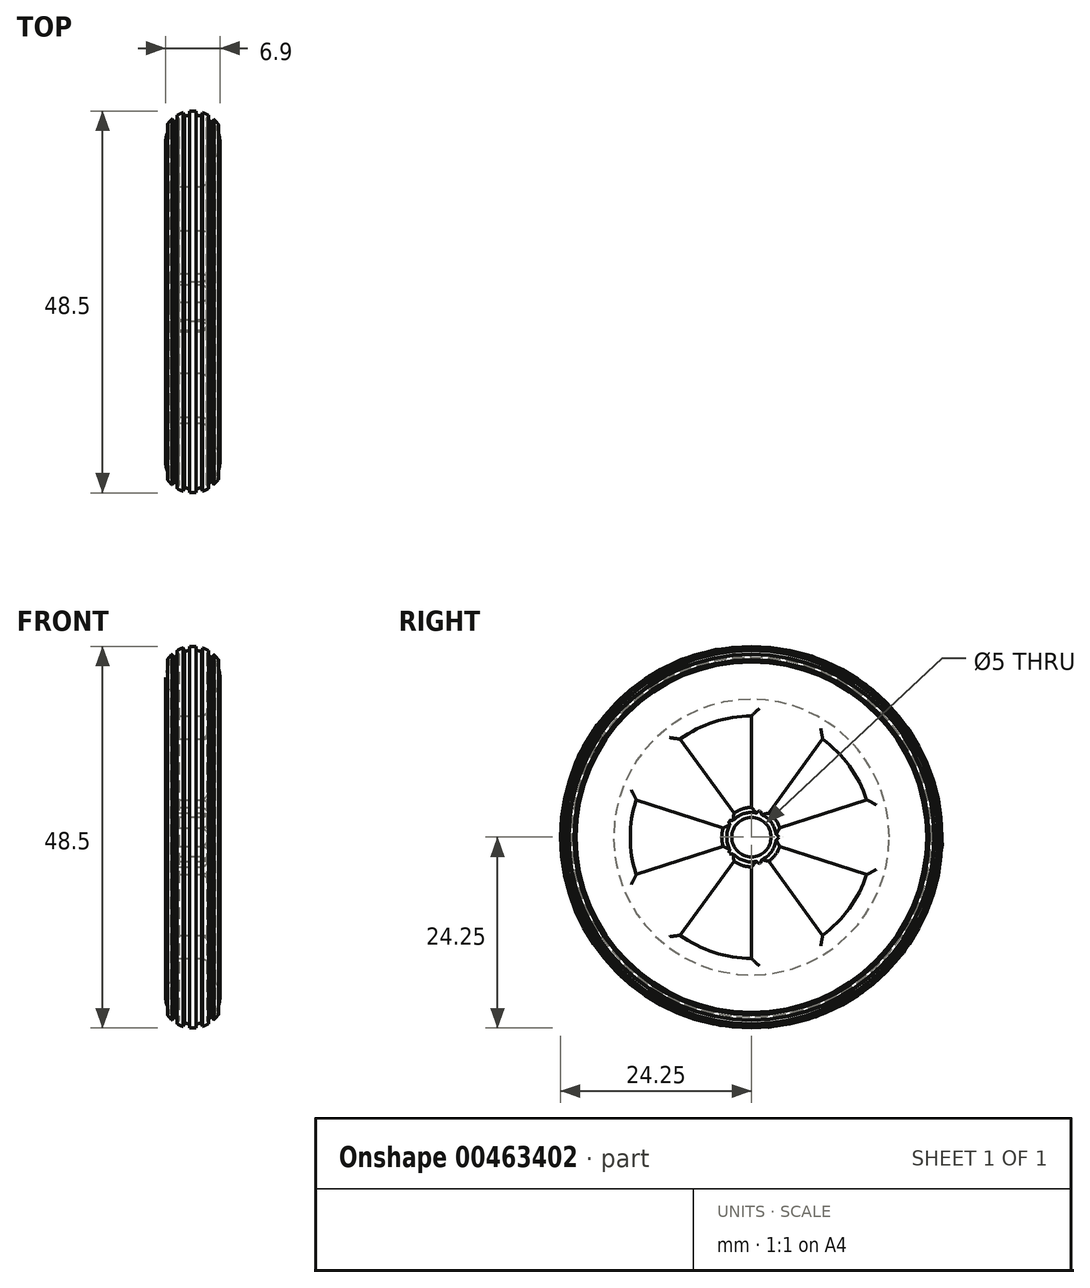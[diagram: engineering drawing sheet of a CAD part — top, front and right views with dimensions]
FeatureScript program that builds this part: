
annotation { "Feature Type Name" : "Feature", "Feature Type Description" : "" }
export const myFeature = defineFeature(function(context is Context, id is Id, definition is map)
    precondition{}
    {
        {
            var Q0;
            Q0=qCreatedBy(makeId("Front.planeOp"),FACE);
            var sketch = newSketch(context, id + "F0", { "sketchPlane" : qUnion([Q0])});
            skLineSegment(sketch, "E0", {"start": v(0, 0) * mm, "end": v(0, 2.5) * mm});
            skLineSegment(sketch, "E1", {"start": v(0, 2.5) * mm, "end": v(4, 2.5) * mm});
            skLineSegment(sketch, "E2", {"start": v(0, 2.5) * mm, "end": v(0, 17.5) * mm});
            skLineSegment(sketch, "E3", {"start": v(4, 2.5) * mm, "end": v(4, 17.5) * mm});
            skArc(sketch, "E4", {"start": v(4, 17.5) * mm, "mid": v(5.4, 19.71) * mm, "end": v(4.84, 22.27) * mm});
            skPoint(sketch, "E4.third.point", {"position": v(4, 23.12) * mm});
            skArc(sketch, "E5", {"start": v(-0.65, 23.22) * mm, "mid": v(-0.95, 22.92) * mm, "end": v(-1.21, 22.6) * mm});
            skLineSegment(sketch, "E6", {"start": v(-0.8, 22.3) * mm, "end": v(-1.21, 22.6) * mm});
            skLineSegment(sketch, "E7.1.0", {"start": v(-0.32, 22.86) * mm, "end": v(-0.65, 23.22) * mm});
            skLineSegment(sketch, "E7.2.0", {"start": v(0.27, 23.3) * mm, "end": v(0.02, 23.72) * mm});
            skLineSegment(sketch, "E7.3.0", {"start": v(0.94, 23.59) * mm, "end": v(0.79, 24.06) * mm});
            skLineSegment(sketch, "E7.4.0", {"start": v(1.66, 23.74) * mm, "end": v(1.6, 24.23) * mm});
            skLineSegment(sketch, "E7.5.0", {"start": v(2.4, 23.73) * mm, "end": v(2.45, 24.22) * mm});
            skLineSegment(sketch, "E7.6.0", {"start": v(3.1, 23.57) * mm, "end": v(3.27, 24.04) * mm});
            skLineSegment(sketch, "E7.7.0", {"start": v(3.77, 23.26) * mm, "end": v(4.03, 23.69) * mm});
            skLineSegment(sketch, "E7.8.0", {"start": v(4.36, 22.82) * mm, "end": v(4.7, 23.18) * mm});
            skLineSegment(sketch, "E7.9.0", {"start": v(4.84, 22.27) * mm, "end": v(5.24, 22.54) * mm});
            skLineSegment(sketch, "E7.anchor1", {"start": v(-0.8, 22.3) * mm, "end": v(-1.21, 22.6) * mm, "construction": true});
            skLineSegment(sketch, "E7.anchor2", {"start": v(4.84, 22.27) * mm, "end": v(5.24, 22.54) * mm, "construction": true});
            skArc(sketch, "E8.trimOffspring", {"start": v(0.79, 24.06) * mm, "mid": v(0.4, 23.9) * mm, "end": v(0.02, 23.72) * mm});
            skArc(sketch, "E9.trimOffspring", {"start": v(2.45, 24.22) * mm, "mid": v(2.03, 24.25) * mm, "end": v(1.6, 24.23) * mm});
            skArc(sketch, "E10.trimOffspring", {"start": v(4.03, 23.69) * mm, "mid": v(3.66, 23.88) * mm, "end": v(3.27, 24.04) * mm});
            skArc(sketch, "E11.trimOffspring", {"start": v(-0.8, 22.3) * mm, "mid": v(-1.4, 19.74) * mm, "end": v(0, 17.5) * mm});
            skArc(sketch, "E12.trimOffspring", {"start": v(0.27, 23.3) * mm, "mid": v(-0.04, 23.09) * mm, "end": v(-0.32, 22.86) * mm});
            skArc(sketch, "E13.trimOffspring", {"start": v(1.66, 23.74) * mm, "mid": v(1.3, 23.68) * mm, "end": v(0.94, 23.59) * mm});
            skArc(sketch, "E14.trimOffspring", {"start": v(3.1, 23.57) * mm, "mid": v(2.75, 23.67) * mm, "end": v(2.4, 23.73) * mm});
            skArc(sketch, "E15.trimOffspring", {"start": v(4.36, 22.82) * mm, "mid": v(4.08, 23.06) * mm, "end": v(3.77, 23.26) * mm});
            skArc(sketch, "E16.trimOffspring", {"start": v(5.24, 22.54) * mm, "mid": v(4.99, 22.88) * mm, "end": v(4.7, 23.18) * mm});
            skLineSegment(sketch, "E17", {"start": v(0, 0) * mm, "end": v(4.13, 0) * mm});
            skSolve(sketch);
        }
        {
            var Q0;
            Q0=makeQuery(id+"F0.imprint","IMPRINT",FACE,{"disambiguationData":[TD([[makeQuery(id+"F0.imprint","IMPRINT",EDGE,{"derivedFrom":sQuery(id+"F0.wireOp",EDGE,"E1")}),1.0]])]});
            var Q1;
            Q1=sQuery(id+"F0.wireOp",EDGE,"E17");
            revolve(context, id + "F1", {"entities" : qUnion([Q0]), "axis" : qUnion([Q1]), "revolveType" : RevolveType.FULL});
        }
        {
            var Q0;
            Q0=makeQuery(id+"F1.opRevolve","SWEPT_FACE",FACE,{"disambiguationData":[OSD([sQuery(id+"F0.wireOp",EDGE,"E3")])]});
            var sketch = newSketch(context, id + "F2", { "sketchPlane" : qUnion([Q0])});
            skArc(sketch, "E18", {"start": v(0, 15.39) * mm, "mid": v(-4.76, 14.64) * mm, "end": v(-9.05, 12.45) * mm});
            skArc(sketch, "E19", {"start": v(0, 3.77) * mm, "mid": v(-1.17, 3.59) * mm, "end": v(-2.22, 3.05) * mm});
            skLineSegment(sketch, "E20", {"start": v(0, 3.77) * mm, "end": v(0, 15.39) * mm});
            skLineSegment(sketch, "E21.1.0", {"start": v(-2.22, 3.05) * mm, "end": v(-9.05, 12.45) * mm});
            skLineSegment(sketch, "E21.2.0", {"start": v(-3.59, 1.17) * mm, "end": v(-14.64, 4.76) * mm});
            skLineSegment(sketch, "E21.3.0", {"start": v(-3.59, -1.17) * mm, "end": v(-14.64, -4.76) * mm});
            skLineSegment(sketch, "E21.4.0", {"start": v(-2.22, -3.05) * mm, "end": v(-9.05, -12.45) * mm});
            skLineSegment(sketch, "E21.5.0", {"start": v(0, -3.77) * mm, "end": v(0, -15.39) * mm});
            skLineSegment(sketch, "E21.6.0", {"start": v(2.22, -3.05) * mm, "end": v(9.05, -12.45) * mm});
            skLineSegment(sketch, "E21.7.0", {"start": v(3.59, -1.17) * mm, "end": v(14.64, -4.76) * mm});
            skLineSegment(sketch, "E21.8.0", {"start": v(3.59, 1.17) * mm, "end": v(14.64, 4.76) * mm});
            skLineSegment(sketch, "E21.9.0", {"start": v(2.22, 3.05) * mm, "end": v(9.05, 12.45) * mm});
            skArc(sketch, "E22.trimOffspring", {"start": v(3.59, 1.17) * mm, "mid": v(3.05, 2.22) * mm, "end": v(2.22, 3.05) * mm});
            skArc(sketch, "E23.trimOffspring", {"start": v(14.64, 4.76) * mm, "mid": v(12.45, 9.05) * mm, "end": v(9.05, 12.45) * mm});
            skArc(sketch, "E24.trimOffspring", {"start": v(2.22, -3.05) * mm, "mid": v(3.05, -2.22) * mm, "end": v(3.59, -1.17) * mm});
            skArc(sketch, "E25.trimOffspring", {"start": v(9.05, -12.45) * mm, "mid": v(12.45, -9.05) * mm, "end": v(14.64, -4.76) * mm});
            skArc(sketch, "E26.trimOffspring", {"start": v(-2.22, -3.05) * mm, "mid": v(-1.17, -3.59) * mm, "end": v(0, -3.77) * mm});
            skArc(sketch, "E27.trimOffspring", {"start": v(-9.05, -12.45) * mm, "mid": v(-4.76, -14.64) * mm, "end": v(0, -15.39) * mm});
            skArc(sketch, "E28.trimOffspring", {"start": v(-3.59, 1.17) * mm, "mid": v(-3.77, 0) * mm, "end": v(-3.59, -1.17) * mm});
            skArc(sketch, "E29.trimOffspring", {"start": v(-14.64, 4.76) * mm, "mid": v(-15.39, 0) * mm, "end": v(-14.64, -4.76) * mm});
            skSolve(sketch);
        }
        {
            var Q0;
            Q0 = qSketchRegion(id + "F2", true);
            extrude(context, id + "F3", {"entities" : qUnion([Q0]), "operationType" : NewBodyOperationType.REMOVE, "oppositeDirection" : true, "depth" : 4 * mm});
        }
        {
            var Q0;
            Q0=makeQuery(id+"F3.boolean.opBoolean","COPY",EDGE,{"derivedFrom":makeQuery(id+"F3.opExtrude","CAP_EDGE",EDGE,{"disambiguationData":[OSD([sQuery(id+"F2.wireOp",EDGE,"E29.trimOffspring")])],"isStart":true})});
            var Q1;
            Q1=makeQuery(id+"F3.boolean.opBoolean","COPY",EDGE,{"derivedFrom":makeQuery(id+"F3.opExtrude","CAP_EDGE",EDGE,{"disambiguationData":[OSD([sQuery(id+"F2.wireOp",EDGE,"E21.2.0")])],"isStart":true})});
            var Q2;
            Q2=makeQuery(id+"F3.boolean.opBoolean","COPY",EDGE,{"derivedFrom":makeQuery(id+"F3.opExtrude","CAP_EDGE",EDGE,{"disambiguationData":[OSD([sQuery(id+"F2.wireOp",EDGE,"E21.3.0")])],"isStart":true})});
            var Q3;
            Q3=makeQuery(id+"F3.boolean.opBoolean","COPY",EDGE,{"derivedFrom":makeQuery(id+"F3.opExtrude","CAP_EDGE",EDGE,{"disambiguationData":[OSD([sQuery(id+"F2.wireOp",EDGE,"E21.1.0")])],"isStart":true})});
            var Q4;
            Q4=makeQuery(id+"F3.boolean.opBoolean","COPY",EDGE,{"derivedFrom":makeQuery(id+"F3.opExtrude","CAP_EDGE",EDGE,{"disambiguationData":[OSD([sQuery(id+"F2.wireOp",EDGE,"E18")])],"isStart":true})});
            var Q5;
            Q5=makeQuery(id+"F1.opRevolve","SWEPT_FACE",FACE,{"disambiguationData":[OSD([sQuery(id+"F0.wireOp",EDGE,"E3")])]});
            fillet(context, id + "F4", {"entities" : qUnion([Q0, Q1, Q2, Q3, Q4, Q5]), "radius" : 1 * mm, "tangentPropagation" : true, "allowEdgeOverflow" : false});
        }
    });
